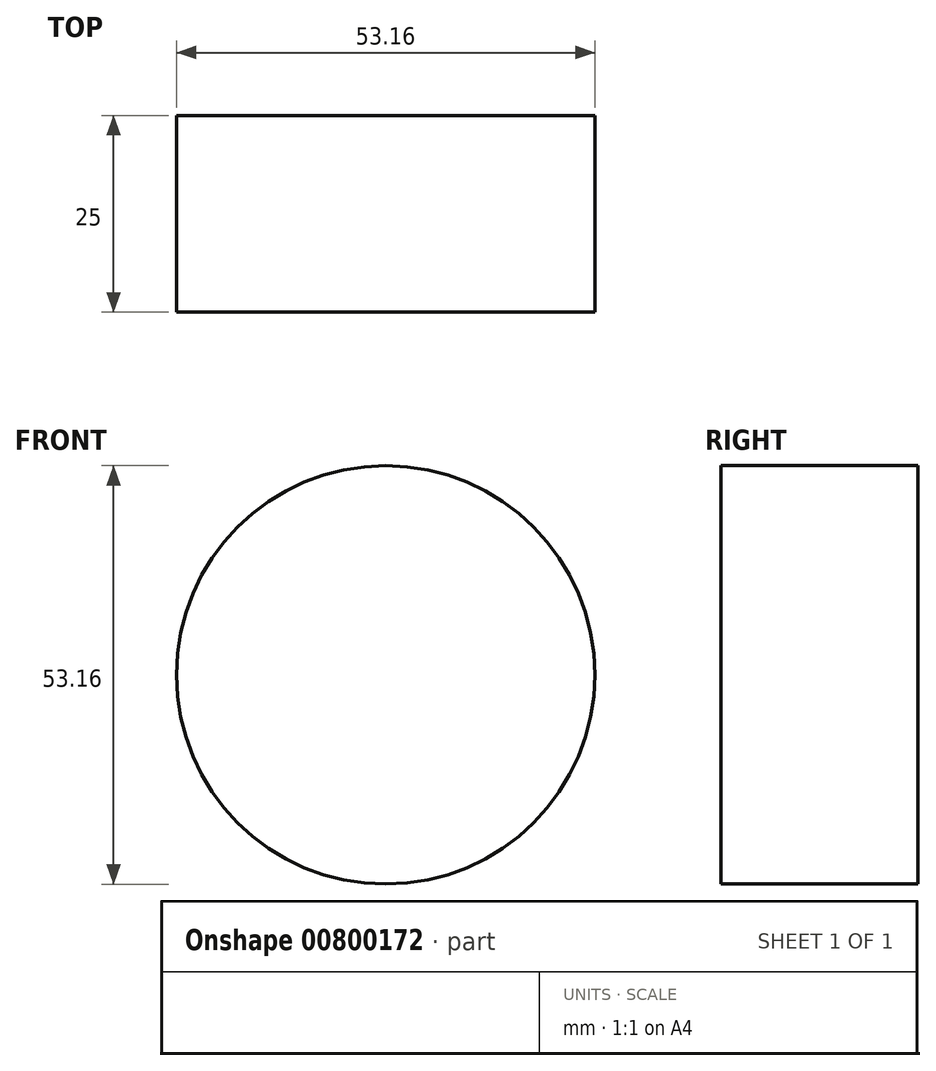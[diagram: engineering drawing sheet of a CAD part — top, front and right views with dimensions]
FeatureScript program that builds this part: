
annotation { "Feature Type Name" : "Feature", "Feature Type Description" : "" }
export const myFeature = defineFeature(function(context is Context, id is Id, definition is map)
    precondition{}
    {
        {
            var Q0;
            Q0=qCreatedBy(makeId("Front.planeOp"),FACE);
            var sketch = newSketch(context, id + "F0", { "sketchPlane" : qUnion([Q0])});
            skCircle(sketch, "E0", {"center": v(0, 0) * mm, "radius": 26.58 * mm});
            skSolve(sketch);
        }
        {
            var Q0;
            Q0 = qSketchRegion(id + "F0", true);
            extrude(context, id + "F1", {"entities" : qUnion([Q0]), "depth" : 25 * mm, "offsetDistance" : 25 * mm});
        }
    });
